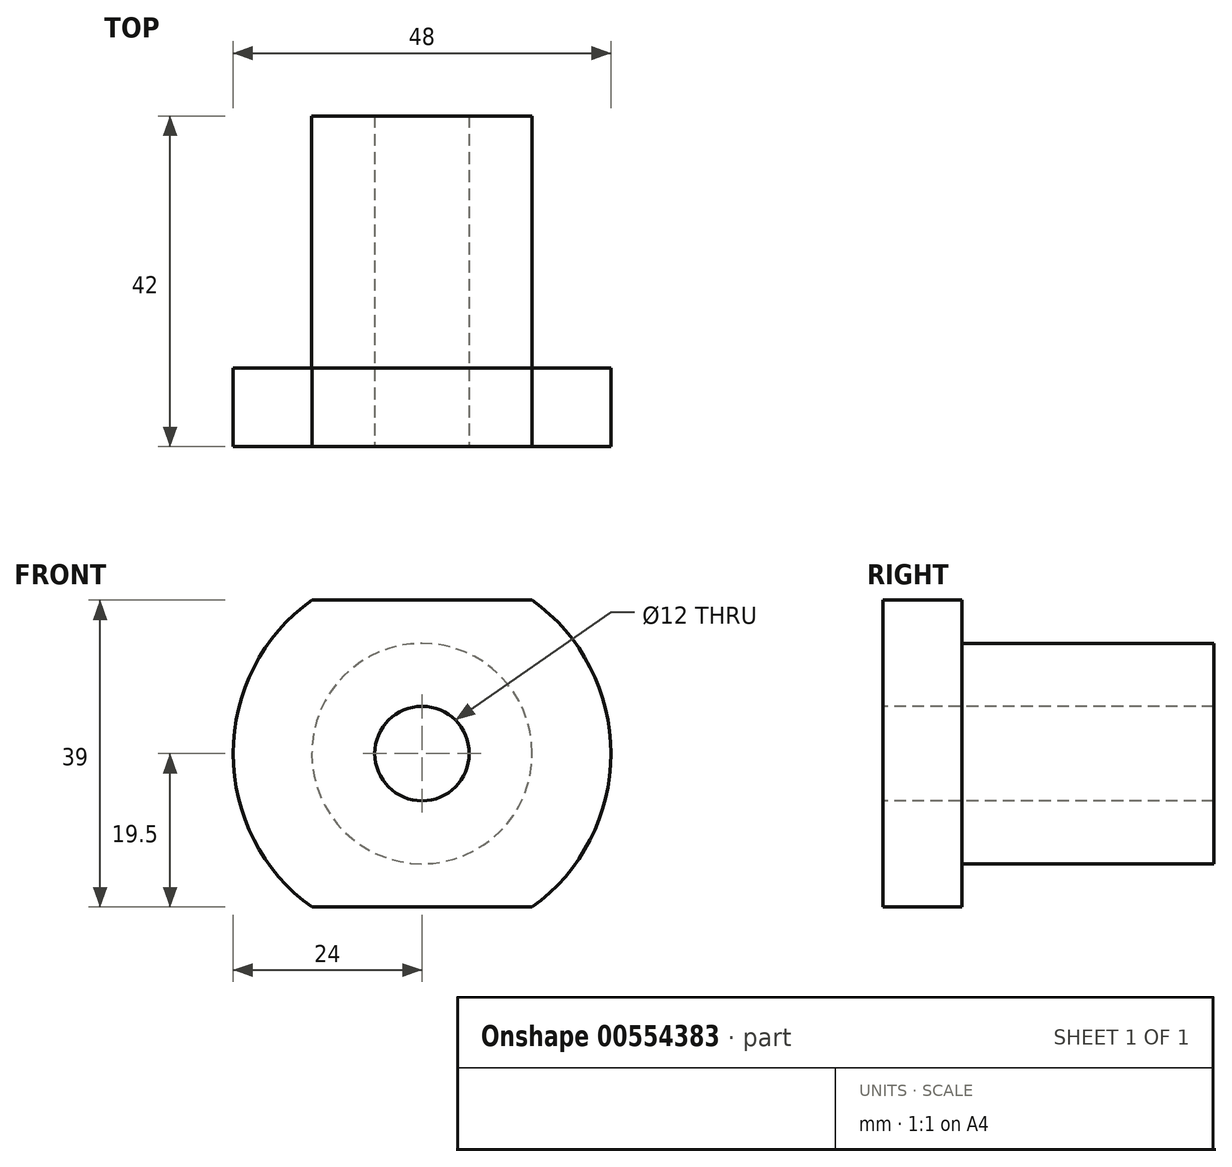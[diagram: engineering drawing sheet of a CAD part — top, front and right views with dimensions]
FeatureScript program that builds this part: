
annotation { "Feature Type Name" : "Feature", "Feature Type Description" : "" }
export const myFeature = defineFeature(function(context is Context, id is Id, definition is map)
    precondition{}
    {
        {
            var Q0;
            Q0=qCreatedBy(makeId("Front.planeOp"),FACE);
            var sketch = newSketch(context, id + "F0", { "sketchPlane" : qUnion([Q0])});
            skCircle(sketch, "E0", {"center": v(0, 0) * mm, "radius": 14 * mm});
            skSolve(sketch);
        }
        {
            var Q0;
            Q0=makeQuery(id+"F0.imprint","IMPRINT",FACE,{"disambiguationData":[TD([[makeQuery(id+"F0.imprint","IMPRINT",EDGE,{"derivedFrom":sQuery(id+"F0.wireOp",EDGE,"E0")}),1.0]])]});
            extrude(context, id + "F1", {"entities" : qUnion([Q0]), "depth" : 42 * mm, "offsetDistance" : 25 * mm});
        }
        {
            var Q0;
            Q0=makeQuery(id+"F1.opExtrude","CAP_FACE",FACE,{"disambiguationData":[OSD([sQuery(id+"F0.wireOp",EDGE,"E0")])],"isStart":false});
            var sketch = newSketch(context, id + "F2", { "sketchPlane" : qUnion([Q0])});
            skCircle(sketch, "E1", {"center": v(0, 0) * mm, "radius": 6 * mm});
            skSolve(sketch);
        }
        {
            var Q0;
            Q0=makeQuery(id+"F2.imprint","IMPRINT",FACE,{"disambiguationData":[TD([[makeQuery(id+"F2.imprint","IMPRINT",EDGE,{"derivedFrom":sQuery(id+"F2.wireOp",EDGE,"E1")}),1.0]])]});
            extrude(context, id + "F3", {"entities" : qUnion([Q0]), "operationType" : NewBodyOperationType.REMOVE, "endBound" : BoundingType.UP_TO_NEXT, "oppositeDirection" : true, "depth" : 25 * mm, "offsetDistance" : 25 * mm});
        }
        {
            var Q0;
            Q0=makeQuery(id+"F1.opExtrude","CAP_FACE",FACE,{"disambiguationData":[OSD([sQuery(id+"F0.wireOp",EDGE,"E0")])],"isStart":false});
            var sketch = newSketch(context, id + "F4", { "sketchPlane" : qUnion([Q0])});
            skCircle(sketch, "E2", {"center": v(0, 0) * mm, "radius": 24 * mm});
            skSolve(sketch);
        }
        {
            var Q0;
            Q0=makeQuery(id+"F4.imprint","IMPRINT",FACE,{"disambiguationData":[TD([[makeQuery(id+"F4.imprint","IMPRINT",EDGE,{"derivedFrom":sQuery(id+"F4.wireOp",EDGE,"E2")}),1.0]])]});
            extrude(context, id + "F5", {"entities" : qUnion([Q0]), "operationType" : NewBodyOperationType.ADD, "oppositeDirection" : true, "depth" : 10 * mm, "offsetDistance" : 25 * mm});
        }
        {
            var Q0;
            {var subQ0=sQuery(id+"F0.wireOp",EDGE,"E0");Q0=makeQuery(id+"F5.boolean.opBoolean","MERGE",FACE,{"derivedFrom":[makeQuery(id+"F1.opExtrude","CAP_FACE",FACE,{"disambiguationData":[OSD([subQ0])],"isStart":false}),makeQuery(id+"F5.opExtrude","CAP_FACE",FACE,{"disambiguationData":[OSD([subQ0,sQuery(id+"F4.wireOp",EDGE,"E2")])],"isStart":true})]});}
            var sketch = newSketch(context, id + "F6", { "sketchPlane" : qUnion([Q0])});
            skLineSegment(sketch, "E3.top", {"start": v(-39.4, 19.5) * mm, "end": v(54.15, 19.5) * mm});
            skLineSegment(sketch, "E3.left", {"start": v(-39.4, 0) * mm, "end": v(-39.4, 19.5) * mm});
            skLineSegment(sketch, "E3.right", {"start": v(54.15, 0) * mm, "end": v(54.15, 19.5) * mm});
            skLineSegment(sketch, "E4.MirrorCS", {"start": v(-39.4, -19.5) * mm, "end": v(54.15, -19.5) * mm});
            skLineSegment(sketch, "E5.MirrorCS", {"start": v(54.15, 0) * mm, "end": v(54.15, -19.5) * mm});
            skLineSegment(sketch, "E6.MirrorCS", {"start": v(-39.4, 0) * mm, "end": v(-39.4, -19.5) * mm});
            skSolve(sketch);
        }
        {
            var Q0;
            {var subQ0=sQuery(id+"F6.wireOp",EDGE,"E3.top");var subQ1=makeQuery(id+"F5.opExtrude","CAP_EDGE",EDGE,{"disambiguationData":[OSD([sQuery(id+"F4.wireOp",EDGE,"E2")])],"isStart":true});var subQ2=makeQuery(id+"F6.imprint","INTERSECT",VERTEX,{"disambiguationData":[OD(0.0)],"derivedFrom":[subQ1,subQ0]});Q0=makeQuery(id+"F6.imprint","IMPRINT",FACE,{"disambiguationData":[TD([[makeQuery(id+"F6.imprint","IMPRINT",EDGE,{"disambiguationData":[TD([[subQ2,-1.0]])],"derivedFrom":subQ0}),1.0]])]});}
            var Q1;
            {var subQ0=sQuery(id+"F6.wireOp",EDGE,"E4.MirrorCS");var subQ1=makeQuery(id+"F5.opExtrude","CAP_EDGE",EDGE,{"disambiguationData":[OSD([sQuery(id+"F4.wireOp",EDGE,"E2")])],"isStart":true});var subQ2=makeQuery(id+"F6.imprint","INTERSECT",VERTEX,{"disambiguationData":[OD(0.0)],"derivedFrom":[subQ1,subQ0]});Q1=makeQuery(id+"F6.imprint","IMPRINT",FACE,{"disambiguationData":[TD([[makeQuery(id+"F6.imprint","IMPRINT",EDGE,{"disambiguationData":[TD([[subQ2,-1.0]])],"derivedFrom":subQ0}),-1.0]])]});}
            extrude(context, id + "F7", {"entities" : qUnion([Q0, Q1]), "operationType" : NewBodyOperationType.REMOVE, "endBound" : BoundingType.UP_TO_NEXT, "oppositeDirection" : true, "depth" : 25 * mm, "offsetDistance" : 25 * mm});
        }
    });
